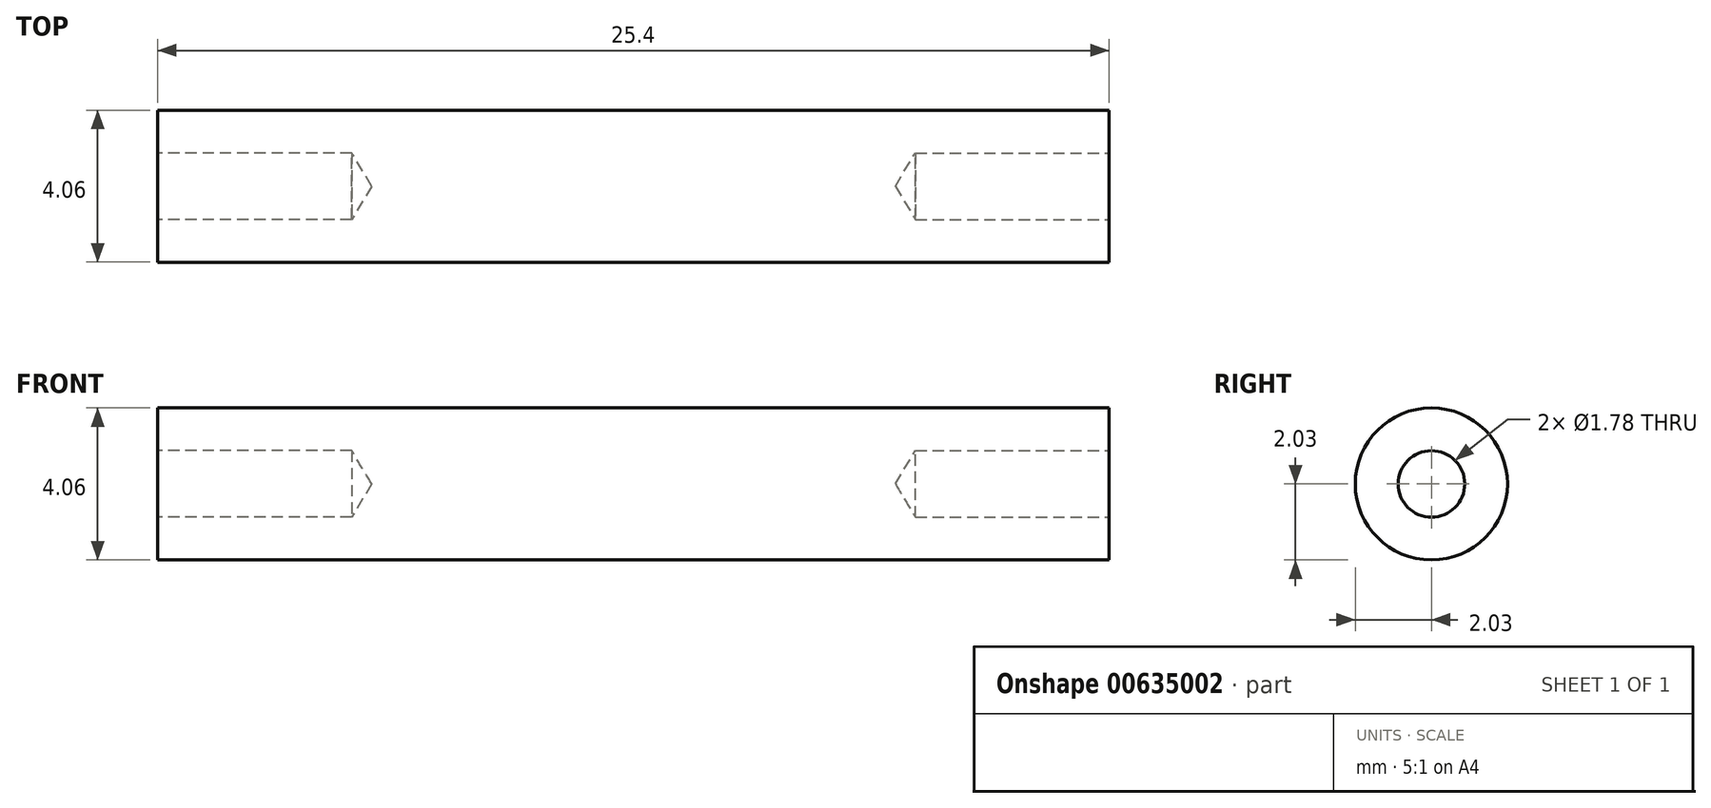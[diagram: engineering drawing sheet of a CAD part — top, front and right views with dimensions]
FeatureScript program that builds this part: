
annotation { "Feature Type Name" : "Feature", "Feature Type Description" : "" }
export const myFeature = defineFeature(function(context is Context, id is Id, definition is map)
    precondition{}
    {
        {
            var Q0;
            Q0=qCreatedBy(makeId("Right.planeOp"),FACE);
            var sketch = newSketch(context, id + "F0", { "sketchPlane" : qUnion([Q0])});
            skCircle(sketch, "E0", {"center": v(0, 0) * mm, "radius": 2.03 * mm});
            skSolve(sketch);
        }
        {
            var Q0;
            Q0 = qSketchRegion(id + "F0", true);
            extrude(context, id + "F1", {"entities" : qUnion([Q0]), "endBound" : BoundingType.SYMMETRIC, "depth" : 25.4 * mm, "offsetDistance" : 25.4 * mm});
        }
        {
            var Q0;
            Q0=makeQuery(id+"F1.opExtrude","CAP_FACE",FACE,{"disambiguationData":[OSD([sQuery(id+"F0.wireOp",EDGE,"E0")])],"isStart":false});
            var sketch = newSketch(context, id + "F2", { "sketchPlane" : qUnion([Q0])});
            skPoint(sketch, "E1", {"position": v(0, 0) * mm});
            skSolve(sketch);
        }
        {
            var Q0;
            Q0=sQuery(id+"F2.wireOp",VERTEX,"E1");
            var Q1;
            Q1=makeQuery(id+"F1.opExtrude","SWEPT_BODY",BODY,{"disambiguationData":[OSD([sQuery(id+"F0.wireOp",EDGE,"E0")])]});
            hole(context, id + "F3", {"style" : HoleStyle.SIMPLE, "endStyle" : HoleEndStyle.BLIND, "standardTappedOrClearance" : lookupTablePath({ "standard" : "ANSI", "engagement" : "75%", "pitch" : "56 tpi", "size" : "#2", "type" : "Tapped" }), "standardBlindInLast" : lookupTablePath({ "standard" : "ANSI", "engagement" : "75%", "pitch" : "56 tpi", "size" : "#2", "type" : "Tapped" }), "holeDiameter" : 1.78 * mm, "majorDiameter" : 2.18 * mm, "showTappedDepth" : true, "holeDepth" : 5.17 * mm, "tappedDepth" : 3.8 * mm, "tapClearance" : 3, "locations" : qUnion([Q0]), "scope" : qUnion([Q1])});
        }
        {
            var Q0;
            Q0=makeQuery(id+"F1.opExtrude","CAP_FACE",FACE,{"disambiguationData":[OSD([sQuery(id+"F0.wireOp",EDGE,"E0")])],"isStart":true});
            var sketch = newSketch(context, id + "F4", { "sketchPlane" : qUnion([Q0])});
            skPoint(sketch, "E2", {"position": v(0, 0) * mm});
            skSolve(sketch);
        }
        {
            var Q0;
            Q0=sQuery(id+"F4.wireOp",VERTEX,"E2");
            var Q1;
            Q1=makeQuery(id+"F1.opExtrude","SWEPT_BODY",BODY,{"disambiguationData":[OSD([sQuery(id+"F0.wireOp",EDGE,"E0")])]});
            hole(context, id + "F5", {"style" : HoleStyle.SIMPLE, "endStyle" : HoleEndStyle.BLIND, "standardTappedOrClearance" : lookupTablePath({ "standard" : "ANSI", "engagement" : "75%", "pitch" : "56 tpi", "size" : "#2", "type" : "Tapped" }), "standardBlindInLast" : lookupTablePath({ "standard" : "ANSI", "engagement" : "75%", "pitch" : "56 tpi", "size" : "#2", "type" : "Tapped" }), "holeDiameter" : 1.78 * mm, "majorDiameter" : 2.18 * mm, "showTappedDepth" : true, "holeDepth" : 5.18 * mm, "tappedDepth" : 3.82 * mm, "tapClearance" : 3, "locations" : qUnion([Q0]), "scope" : qUnion([Q1])});
        }
    });
